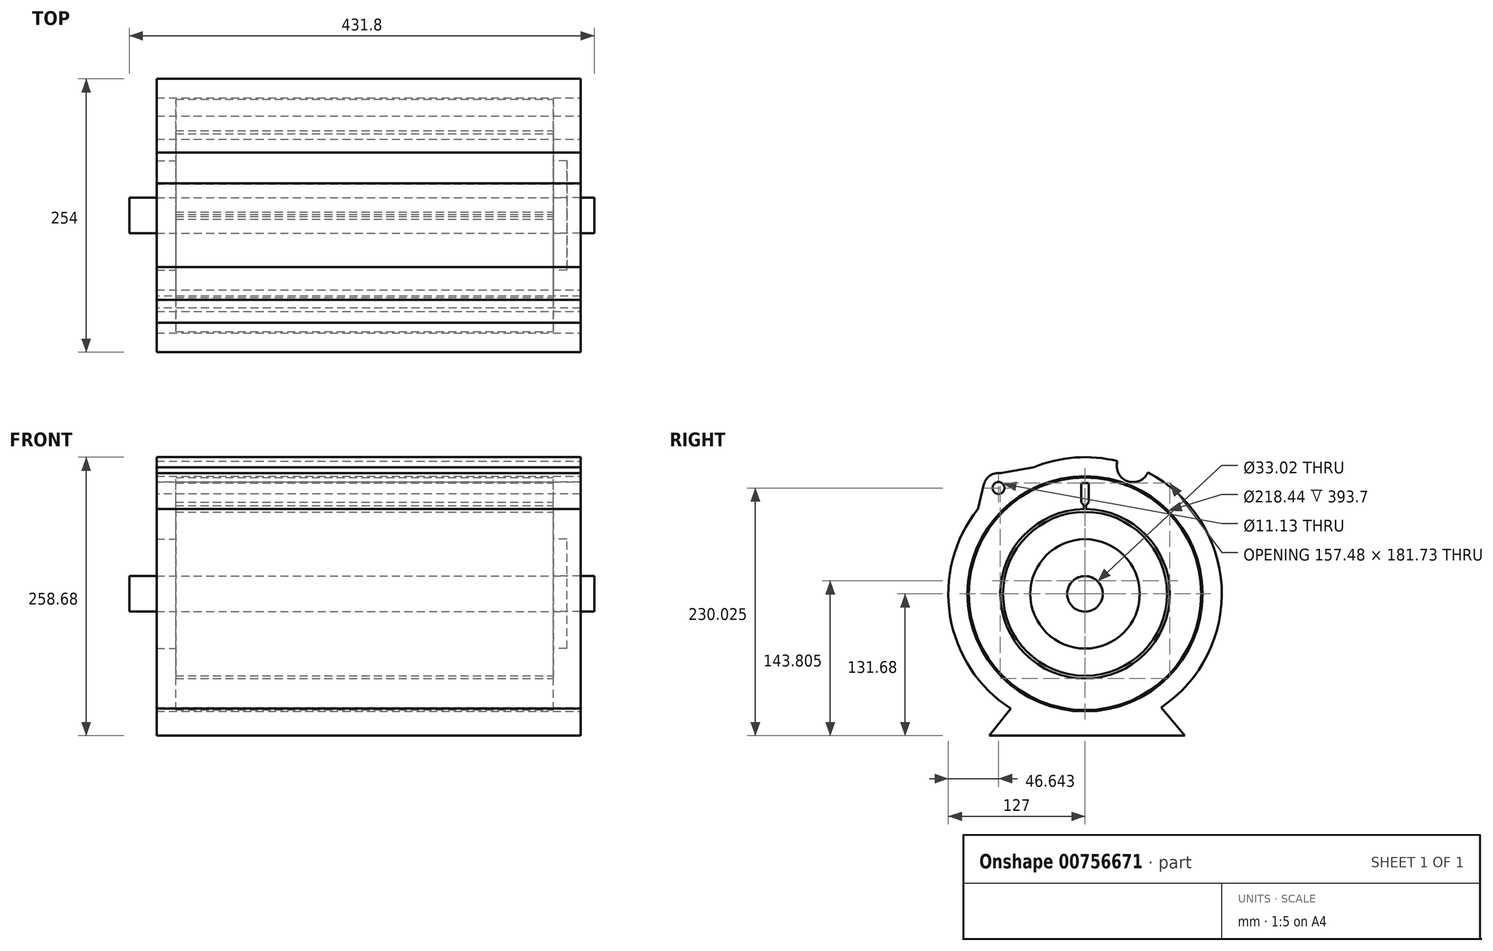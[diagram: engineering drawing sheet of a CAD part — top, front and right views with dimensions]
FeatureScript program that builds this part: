
annotation { "Feature Type Name" : "Feature", "Feature Type Description" : "" }
export const myFeature = defineFeature(function(context is Context, id is Id, definition is map)
    precondition{}
    {
        {
            var Q0;
            Q0=qCreatedBy(makeId("Right.planeOp"),FACE);
            var sketch = newSketch(context, id + "F0", { "sketchPlane" : qUnion([Q0])});
            skCircle(sketch, "E0", {"center": v(0, 0) * mm, "radius": 107.95 * mm});
            skCircle(sketch, "E1", {"center": v(0, 0) * mm, "radius": 78.74 * mm});
            skSolve(sketch);
        }
        {
            var Q0;
            Q0=makeQuery(id+"F0.imprint","IMPRINT",FACE,{"disambiguationData":[TD([[makeQuery(id+"F0.imprint","IMPRINT",EDGE,{"derivedFrom":sQuery(id+"F0.wireOp",EDGE,"E0")}),1.0]])]});
            extrude(context, id + "F1", {"entities" : qUnion([Q0]), "oppositeDirection" : true, "depth" : 350.52 * mm, "offsetDistance" : 25.4 * mm});
        }
        {
            var Q0;
            Q0=makeQuery(id+"F1.opExtrude","CAP_FACE",FACE,{"disambiguationData":[OSD([sQuery(id+"F0.wireOp",EDGE,"E0"),sQuery(id+"F0.wireOp",EDGE,"E1")])],"isStart":true});
            var sketch = newSketch(context, id + "F2", { "sketchPlane" : qUnion([Q0])});
            skCircle(sketch, "E2", {"center": v(0, 0) * mm, "radius": 102.99 * mm});
            skLineSegment(sketch, "E3", {"start": v(0, 78.74) * mm, "end": v(0, 102.99) * mm});
            skLineSegment(sketch, "E4", {"start": v(0.97, 78.73) * mm, "end": v(0.97, 81.94) * mm});
            skLineSegment(sketch, "E5", {"start": v(0.97, 81.94) * mm, "end": v(3.4, 85.13) * mm});
            skLineSegment(sketch, "E6", {"start": v(3.4, 85.13) * mm, "end": v(3.4, 102.93) * mm});
            skLineSegment(sketch, "E7.MirrorCS", {"start": v(-3.4, 85.13) * mm, "end": v(-3.4, 102.93) * mm});
            skLineSegment(sketch, "E8.MirrorCS", {"start": v(-0.97, 81.94) * mm, "end": v(-3.4, 85.13) * mm});
            skLineSegment(sketch, "E9.MirrorCS", {"start": v(-0.97, 78.73) * mm, "end": v(-0.97, 81.94) * mm});
            skSolve(sketch);
        }
        {
            var Q0;
            {var subQ1=sQuery(id+"F2.wireOp",EDGE,"E3");Q0=makeQuery(id+"F2.imprint","IMPRINT",FACE,{"disambiguationData":[TD([[makeQuery(id+"F2.imprint","IMPRINT",EDGE,{"derivedFrom":subQ1}),1.0]])]});}
            var Q1;
            {var subQ1=sQuery(id+"F2.wireOp",EDGE,"E3");Q1=makeQuery(id+"F2.imprint","IMPRINT",FACE,{"disambiguationData":[TD([[makeQuery(id+"F2.imprint","IMPRINT",EDGE,{"derivedFrom":subQ1}),-1.0]])]});}
            extrude(context, id + "F3", {"entities" : qUnion([Q0, Q1]), "operationType" : NewBodyOperationType.REMOVE, "oppositeDirection" : true, "depth" : 350.52 * mm, "offsetDistance" : 25.4 * mm});
        }
        {
            var Q0;
            Q0=qCreatedBy(makeId("Right.planeOp"),FACE);
            var sketch = newSketch(context, id + "F4", { "sketchPlane" : qUnion([Q0])});
            skCircle(sketch, "E10", {"center": v(0, 0) * mm, "radius": 76.13 * mm});
            skCircle(sketch, "E11", {"center": v(0, 0) * mm, "radius": 50.8 * mm});
            skCircle(sketch, "E12", {"center": v(0, 0) * mm, "radius": 16.51 * mm});
            skSolve(sketch);
        }
        {
            var Q0;
            Q0=makeQuery(id+"F4.imprint","IMPRINT",FACE,{"disambiguationData":[TD([[makeQuery(id+"F4.imprint","IMPRINT",EDGE,{"derivedFrom":sQuery(id+"F4.wireOp",EDGE,"E10")}),1.0]])]});
            extrude(context, id + "F5", {"entities" : qUnion([Q0]), "oppositeDirection" : true, "depth" : 350.52 * mm, "offsetDistance" : 25.4 * mm});
        }
        {
            var Q0;
            Q0=makeQuery(id+"F4.imprint","IMPRINT",FACE,{"disambiguationData":[TD([[makeQuery(id+"F4.imprint","IMPRINT",EDGE,{"derivedFrom":sQuery(id+"F4.wireOp",EDGE,"E11")}),1.0]])]});
            extrude(context, id + "F6", {"entities" : qUnion([Q0]), "operationType" : NewBodyOperationType.ADD, "oppositeDirection" : true, "depth" : 368.3 * mm, "offsetDistance" : 25.4 * mm});
        }
        {
            var Q0;
            Q0=makeQuery(id+"F4.imprint","IMPRINT",FACE,{"disambiguationData":[TD([[makeQuery(id+"F4.imprint","IMPRINT",EDGE,{"derivedFrom":sQuery(id+"F4.wireOp",EDGE,"E11")}),1.0]])]});
            extrude(context, id + "F7", {"entities" : qUnion([Q0]), "operationType" : NewBodyOperationType.ADD, "depth" : 12.7 * mm, "offsetDistance" : 25.4 * mm});
        }
        {
            var Q0;
            Q0=makeQuery(id+"F4.imprint","IMPRINT",FACE,{"disambiguationData":[TD([[makeQuery(id+"F4.imprint","IMPRINT",EDGE,{"derivedFrom":sQuery(id+"F4.wireOp",EDGE,"E12")}),1.0]])]});
            extrude(context, id + "F8", {"entities" : qUnion([Q0]), "depth" : 38.1 * mm, "offsetDistance" : 25.4 * mm});
        }
        {
            var Q0;
            Q0=makeQuery(id+"F4.imprint","IMPRINT",FACE,{"disambiguationData":[TD([[makeQuery(id+"F4.imprint","IMPRINT",EDGE,{"derivedFrom":sQuery(id+"F4.wireOp",EDGE,"E12")}),1.0]])]});
            extrude(context, id + "F9", {"entities" : qUnion([Q0]), "oppositeDirection" : true, "depth" : 393.7 * mm, "offsetDistance" : 25.4 * mm});
        }
        {
            var Q0;
            Q0=qCreatedBy(makeId("Right.planeOp"),FACE);
            var sketch = newSketch(context, id + "F10", { "sketchPlane" : qUnion([Q0])});
            skCircle(sketch, "E13", {"center": v(0, 0) * mm, "radius": 127 * mm});
            skCircle(sketch, "E14", {"center": v(0, 0) * mm, "radius": 109.22 * mm});
            skCircle(sketch, "E15", {"center": v(-80.36, 98.35) * mm, "radius": 13.97 * mm});
            skCircle(sketch, "E16", {"center": v(44.53, 118.94) * mm, "radius": 15.14 * mm});
            skLineSegment(sketch, "E17", {"start": v(-99.46, 78.97) * mm, "end": v(-93.93, 101.65) * mm});
            skLineSegment(sketch, "E18", {"start": v(-78.37, 112.18) * mm, "end": v(-47.7, 117.7) * mm});
            skLineSegment(sketch, "E19", {"start": v(-68.96, -106.65) * mm, "end": v(-89.1, -131.68) * mm});
            skLineSegment(sketch, "E20", {"start": v(-89.1, -131.68) * mm, "end": v(92.52, -131.68) * mm});
            skLineSegment(sketch, "E21", {"start": v(92.52, -131.68) * mm, "end": v(70.75, -105.47) * mm});
            skSolve(sketch);
        }
        {
            var Q0;
            Q0=makeQuery(id+"F10.imprint","IMPRINT",FACE,{"disambiguationData":[TD([[makeQuery(id+"F10.imprint","IMPRINT",EDGE,{"derivedFrom":sQuery(id+"F10.wireOp",EDGE,"E14")}),-1.0]])]});
            var Q1;
            {var subQ0=sQuery(id+"F10.wireOp",EDGE,"E15");var subQ1=sQuery(id+"F10.wireOp",EDGE,"E13");var subQ2=makeQuery(id+"F10.imprint","INTERSECT",VERTEX,{"disambiguationData":[OD(0.0)],"derivedFrom":[subQ1,subQ0]});Q1=makeQuery(id+"F10.imprint","IMPRINT",FACE,{"disambiguationData":[TD([[makeQuery(id+"F10.imprint","IMPRINT",EDGE,{"disambiguationData":[TD([[subQ2,-1.0]])],"derivedFrom":subQ1}),1.0]])]});}
            var Q2;
            {var subQ0=sQuery(id+"F10.wireOp",EDGE,"E15");var subQ1=sQuery(id+"F10.wireOp",EDGE,"E13");var subQ2=makeQuery(id+"F10.imprint","INTERSECT",VERTEX,{"disambiguationData":[OD(0.0)],"derivedFrom":[subQ1,subQ0]});Q2=makeQuery(id+"F10.imprint","IMPRINT",FACE,{"disambiguationData":[TD([[makeQuery(id+"F10.imprint","IMPRINT",EDGE,{"disambiguationData":[TD([[subQ2,-1.0]])],"derivedFrom":subQ1}),-1.0]])]});}
            var Q3;
            {var subQ0=sQuery(id+"F10.wireOp",EDGE,"E19");Q3=makeQuery(id+"F10.imprint","IMPRINT",FACE,{"disambiguationData":[TD([[makeQuery(id+"F10.imprint","IMPRINT",EDGE,{"derivedFrom":subQ0}),1.0]])]});}
            var Q4;
            {var subQ0=sQuery(id+"F10.wireOp",EDGE,"E16");var subQ1=sQuery(id+"F10.wireOp",EDGE,"E13");var subQ2=makeQuery(id+"F10.imprint","INTERSECT",VERTEX,{"disambiguationData":[OD(0.0)],"derivedFrom":[subQ1,subQ0]});Q4=makeQuery(id+"F10.imprint","IMPRINT",FACE,{"disambiguationData":[TD([[makeQuery(id+"F10.imprint","IMPRINT",EDGE,{"disambiguationData":[TD([[subQ2,1.0]])],"derivedFrom":subQ1}),-1.0]])]});}
            var Q5;
            {var subQ0=sQuery(id+"F10.wireOp",EDGE,"E16");var subQ1=sQuery(id+"F10.wireOp",EDGE,"E13");var subQ2=makeQuery(id+"F10.imprint","INTERSECT",VERTEX,{"disambiguationData":[OD(0.0)],"derivedFrom":[subQ1,subQ0]});Q5=makeQuery(id+"F10.imprint","IMPRINT",FACE,{"disambiguationData":[TD([[makeQuery(id+"F10.imprint","IMPRINT",EDGE,{"disambiguationData":[TD([[subQ2,1.0]])],"derivedFrom":subQ1}),1.0]])]});}
            var Q6;
            {var subQ0=sQuery(id+"F10.wireOp",EDGE,"E18");Q6=makeQuery(id+"F10.imprint","IMPRINT",FACE,{"disambiguationData":[TD([[makeQuery(id+"F10.imprint","IMPRINT",EDGE,{"derivedFrom":subQ0}),-1.0]])]});}
            var Q7;
            {var subQ0=sQuery(id+"F10.wireOp",EDGE,"E17");Q7=makeQuery(id+"F10.imprint","IMPRINT",FACE,{"disambiguationData":[TD([[makeQuery(id+"F10.imprint","IMPRINT",EDGE,{"derivedFrom":subQ0}),-1.0]])]});}
            extrude(context, id + "F11", {"entities" : qUnion([Q0, Q1, Q2, Q3, Q4, Q5, Q6, Q7]), "oppositeDirection" : true, "depth" : 368.3 * mm, "offsetDistance" : 25.4 * mm});
        }
        {
            var Q0;
            Q0=makeQuery(id+"F11.opExtrude","CAP_FACE",FACE,{"disambiguationData":[OSD([sQuery(id+"F10.wireOp",EDGE,"E13"),sQuery(id+"F10.wireOp",EDGE,"E14"),sQuery(id+"F10.wireOp",EDGE,"E15"),sQuery(id+"F10.wireOp",EDGE,"E16"),sQuery(id+"F10.wireOp",EDGE,"E17"),sQuery(id+"F10.wireOp",EDGE,"E18"),sQuery(id+"F10.wireOp",EDGE,"E19"),sQuery(id+"F10.wireOp",EDGE,"E20"),sQuery(id+"F10.wireOp",EDGE,"E21")])],"isStart":true});
            extrude(context, id + "F12", {"entities" : qUnion([Q0]), "operationType" : NewBodyOperationType.ADD, "depth" : 25.4 * mm, "offsetDistance" : 25.4 * mm});
        }
        {
            var Q0;
            Q0=makeQuery(id+"F11.opExtrude","CAP_FACE",FACE,{"disambiguationData":[OSD([sQuery(id+"F10.wireOp",EDGE,"E13"),sQuery(id+"F10.wireOp",EDGE,"E14"),sQuery(id+"F10.wireOp",EDGE,"E15"),sQuery(id+"F10.wireOp",EDGE,"E16"),sQuery(id+"F10.wireOp",EDGE,"E17"),sQuery(id+"F10.wireOp",EDGE,"E18"),sQuery(id+"F10.wireOp",EDGE,"E19"),sQuery(id+"F10.wireOp",EDGE,"E20"),sQuery(id+"F10.wireOp",EDGE,"E21")])],"isStart":false});
            var sketch = newSketch(context, id + "F13", { "sketchPlane" : qUnion([Q0])});
            skCircle(sketch, "E22", {"center": v(-44.53, 118.94) * mm, "radius": 6.62 * mm});
            skCircle(sketch, "E23", {"center": v(80.36, 98.35) * mm, "radius": 5.56 * mm});
            skSolve(sketch);
        }
        {
            var Q0;
            Q0=makeQuery(id+"F13.imprint","IMPRINT",FACE,{"disambiguationData":[TD([[makeQuery(id+"F13.imprint","IMPRINT",EDGE,{"derivedFrom":sQuery(id+"F13.wireOp",EDGE,"E22")}),1.0]])]});
            var Q1;
            Q1=makeQuery(id+"F13.imprint","IMPRINT",FACE,{"disambiguationData":[TD([[makeQuery(id+"F13.imprint","IMPRINT",EDGE,{"derivedFrom":sQuery(id+"F13.wireOp",EDGE,"E23")}),1.0]])]});
            extrude(context, id + "F14", {"entities" : qUnion([Q0, Q1]), "operationType" : NewBodyOperationType.REMOVE, "oppositeDirection" : true, "depth" : 393.7 * mm, "offsetDistance" : 25.4 * mm});
        }
    });
